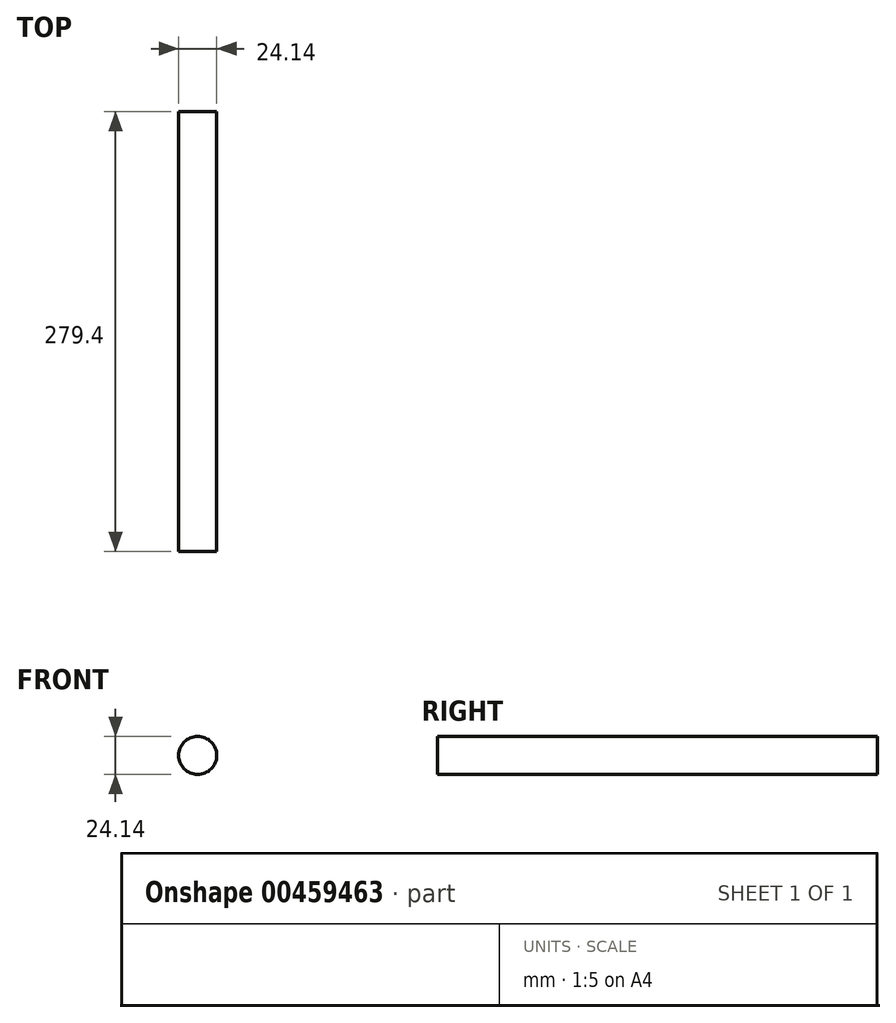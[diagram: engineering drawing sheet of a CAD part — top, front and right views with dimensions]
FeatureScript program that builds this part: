
annotation { "Feature Type Name" : "Feature", "Feature Type Description" : "" }
export const myFeature = defineFeature(function(context is Context, id is Id, definition is map)
    precondition{}
    {
        {
            var Q0;
            Q0=qCreatedBy(makeId("Front.planeOp"),FACE);
            var sketch = newSketch(context, id + "F0", { "sketchPlane" : qUnion([Q0])});
            skCircle(sketch, "E0", {"center": v(0, 0) * mm, "radius": 12.07 * mm});
            skSolve(sketch);
        }
        {
            var Q0;
            Q0=qSketchRegion(id+"F0",true);
            extrude(context, id + "F1", {"entities" : qUnion([Q0]), "depth" : 279.4 * mm});
        }
    });
